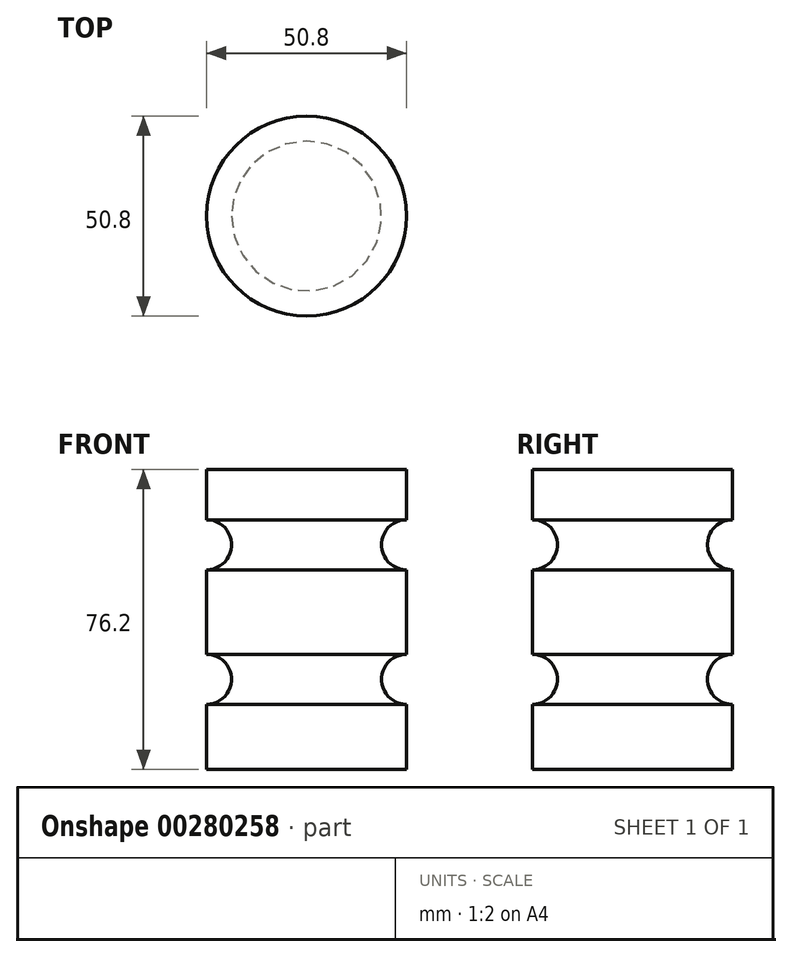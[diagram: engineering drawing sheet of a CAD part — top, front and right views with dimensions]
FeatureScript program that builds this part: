
annotation { "Feature Type Name" : "Feature", "Feature Type Description" : "" }
export const myFeature = defineFeature(function(context is Context, id is Id, definition is map)
    precondition{}
    {
        {
            var Q0;
            Q0=qCreatedBy(makeId("Front.planeOp"),FACE);
            var sketch = newSketch(context, id + "F0", { "sketchPlane" : qUnion([Q0])});
            skLineSegment(sketch, "E0.bottom", {"start": v(0, 0) * mm, "end": v(25.4, 0) * mm});
            skLineSegment(sketch, "E0.top", {"start": v(0, 76.2) * mm, "end": v(25.4, 76.2) * mm});
            skLineSegment(sketch, "E0.left", {"start": v(0, 0) * mm, "end": v(0, 76.2) * mm});
            skLineSegment(sketch, "E0.right", {"start": v(25.4, 0) * mm, "end": v(25.4, 50.75) * mm});
            skLineSegment(sketch, "E1", {"start": v(25.4, 63.45) * mm, "end": v(25.4, 76.2) * mm});
            skLineSegment(sketch, "E2", {"start": v(25.4, 50.75) * mm, "end": v(25.4, 63.45) * mm});
            skArc(sketch, "E3", {"start": v(25.4, 63.45) * mm, "mid": v(19.05, 57.1) * mm, "end": v(25.4, 50.75) * mm});
            skLineSegment(sketch, "E4", {"start": v(25.4, 63.45) * mm, "end": v(25.4, 63.45) * mm});
            skArc(sketch, "E5", {"start": v(25.4, 29.26) * mm, "mid": v(19.05, 22.91) * mm, "end": v(25.4, 16.56) * mm});
            skSolve(sketch);
        }
        {
            var Q0;
            {var subQ1=sQuery(id+"F0.wireOp",EDGE,"E0.bottom");Q0=makeQuery(id+"F0.imprint","IMPRINT",FACE,{"disambiguationData":[TD([[makeQuery(id+"F0.imprint","IMPRINT",EDGE,{"derivedFrom":subQ1}),1.0]])]});}
            var Q1;
            Q1=sQuery(id+"F0.wireOp",EDGE,"E0.left");
            revolve(context, id + "F1", {"entities" : qUnion([Q0]), "axis" : qUnion([Q1]), "revolveType" : RevolveType.FULL});
        }
    });
